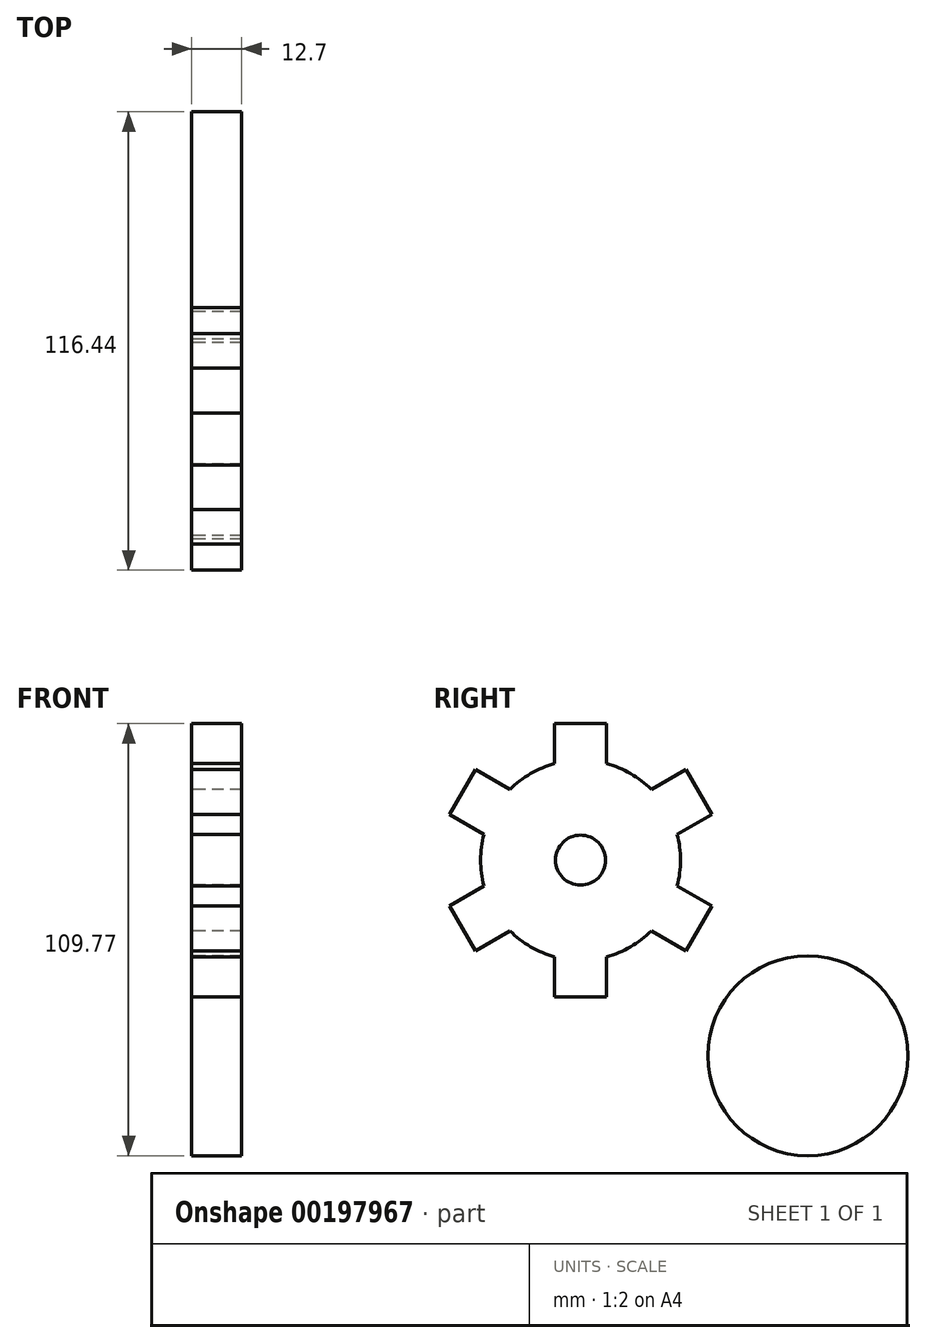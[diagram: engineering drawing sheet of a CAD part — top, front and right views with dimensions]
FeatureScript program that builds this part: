
annotation { "Feature Type Name" : "Feature", "Feature Type Description" : "" }
export const myFeature = defineFeature(function(context is Context, id is Id, definition is map)
    precondition{}
    {
        {
            var Q0;
            Q0=qCreatedBy(makeId("Right.planeOp"),FACE);
            var sketch = newSketch(context, id + "F0", { "sketchPlane" : qUnion([Q0])});
            skCircle(sketch, "E0", {"center": v(0, 0) * mm, "radius": 25.4 * mm});
            skSolve(sketch);
        }
        {
            var Q0;
            Q0 = qSketchRegion(id + "F0", true);
            extrude(context, id + "F1", {"entities" : qUnion([Q0]), "depth" : 12.7 * mm});
        }
        {
            var Q0;
            Q0=makeQuery(id+"F1.opExtrude","CAP_FACE",FACE,{"disambiguationData":[OSD([sQuery(id+"F0.wireOp",EDGE,"E0")])],"isStart":true});
            var sketch = newSketch(context, id + "F2", { "sketchPlane" : qUnion([Q0])});
            skLineSegment(sketch, "E1", {"start": v(0, 0) * mm, "end": v(0, 25.4) * mm});
            skLineSegment(sketch, "E2", {"start": v(0, 0) * mm, "end": v(6.57, 24.53) * mm});
            skLineSegment(sketch, "E3", {"start": v(0, 0) * mm, "end": v(-6.57, 24.53) * mm});
            skLineSegment(sketch, "E4", {"start": v(-6.57, 24.53) * mm, "end": v(6.57, 24.53) * mm});
            skLineSegment(sketch, "E5.0", {"start": v(-6.57, 34.7) * mm, "end": v(6.57, 34.7) * mm});
            skLineSegment(sketch, "E6", {"start": v(-6.57, 34.7) * mm, "end": v(-6.57, 24.53) * mm});
            skLineSegment(sketch, "E7", {"start": v(6.57, 34.7) * mm, "end": v(6.57, 24.53) * mm});
            skSolve(sketch);
        }
        {
            var Q0;
            Q0 = qSketchRegion(id + "F2", true);
            extrude(context, id + "F3", {"entities" : qUnion([Q0]), "operationType" : NewBodyOperationType.ADD, "oppositeDirection" : true, "depth" : 12.7 * mm});
        }
        {
            var Q0;
            Q0=qCreatedBy(makeId("Front.planeOp"),FACE);
            var sketch = newSketch(context, id + "F4", { "sketchPlane" : qUnion([Q0])});
            skLineSegment(sketch, "E8", {"start": v(0, 0) * mm, "end": v(-56.7, 0) * mm});
            skSolve(sketch);
        }
        {
            var Q0;
            Q0=makeQuery(id+"F1.opExtrude","SWEPT_BODY",BODY,{"disambiguationData":[OSD([sQuery(id+"F0.wireOp",EDGE,"E0")])]});
            var Q1;
            Q1=sQuery(id+"F4.wireOp",EDGE,"E8");
            circularPattern(context, id + "F5", {"operationType" : NewBodyOperationType.ADD, "entities" : qUnion([Q0]), "axis" : qUnion([Q1]), "angle" : 360 * degree, "instanceCount" : 6, "equalSpace" : true});
        }
        {
            var Q0;
            {var subQ0=makeQuery(id+"F3.boolean.opBoolean","MERGE",FACE,{"derivedFrom":[makeQuery(id+"F1.opExtrude","CAP_FACE",FACE,{"disambiguationData":[OSD([sQuery(id+"F0.wireOp",EDGE,"E0")])],"isStart":true}),makeQuery(id+"F3.opExtrude","CAP_FACE",FACE,{"disambiguationData":[OSD([sQuery(id+"F2.wireOp",EDGE,"E2"),sQuery(id+"F2.wireOp",EDGE,"E3"),sQuery(id+"F2.wireOp",EDGE,"E5.0"),sQuery(id+"F2.wireOp",EDGE,"E6"),sQuery(id+"F2.wireOp",EDGE,"E7")])],"isStart":true})]});Q0=makeQuery(id+"F5.boolean.opBoolean","MERGE",FACE,{"derivedFrom":[subQ0,makeQuery(id+"F5.opPattern","COPY",FACE,{"derivedFrom":subQ0,"instanceName":"1"}),makeQuery(id+"F5.opPattern","COPY",FACE,{"derivedFrom":subQ0,"instanceName":"2"}),makeQuery(id+"F5.opPattern","COPY",FACE,{"derivedFrom":subQ0,"instanceName":"3"}),makeQuery(id+"F5.opPattern","COPY",FACE,{"derivedFrom":subQ0,"instanceName":"4"}),makeQuery(id+"F5.opPattern","COPY",FACE,{"derivedFrom":subQ0,"instanceName":"5"})]});}
            var sketch = newSketch(context, id + "F6", { "sketchPlane" : qUnion([Q0])});
            skCircle(sketch, "E9", {"center": v(0, 0) * mm, "radius": 6.35 * mm});
            skSolve(sketch);
        }
        {
            var Q0;
            Q0=makeQuery(id+"F6.imprint","IMPRINT",FACE,{"disambiguationData":[TD([[makeQuery(id+"F6.imprint","IMPRINT",EDGE,{"derivedFrom":sQuery(id+"F6.wireOp",EDGE,"E9")}),1.0]])]});
            extrude(context, id + "F7", {"entities" : qUnion([Q0]), "operationType" : NewBodyOperationType.REMOVE, "oppositeDirection" : true, "depth" : 25.4 * mm});
        }
        {
            var Q0;
            Q0=qCreatedBy(makeId("Right.planeOp"),FACE);
            var sketch = newSketch(context, id + "F8", { "sketchPlane" : qUnion([Q0])});
            skCircle(sketch, "E10", {"center": v(57.7, -49.68) * mm, "radius": 25.4 * mm});
            skSolve(sketch);
        }
        {
            var Q0;
            Q0=makeQuery(id+"F8.imprint","IMPRINT",FACE,{"disambiguationData":[TD([[makeQuery(id+"F8.imprint","IMPRINT",EDGE,{"derivedFrom":sQuery(id+"F8.wireOp",EDGE,"E10")}),1.0]])]});
            extrude(context, id + "F9", {"entities" : qUnion([Q0]), "depth" : 12.7 * mm});
        }
    });
